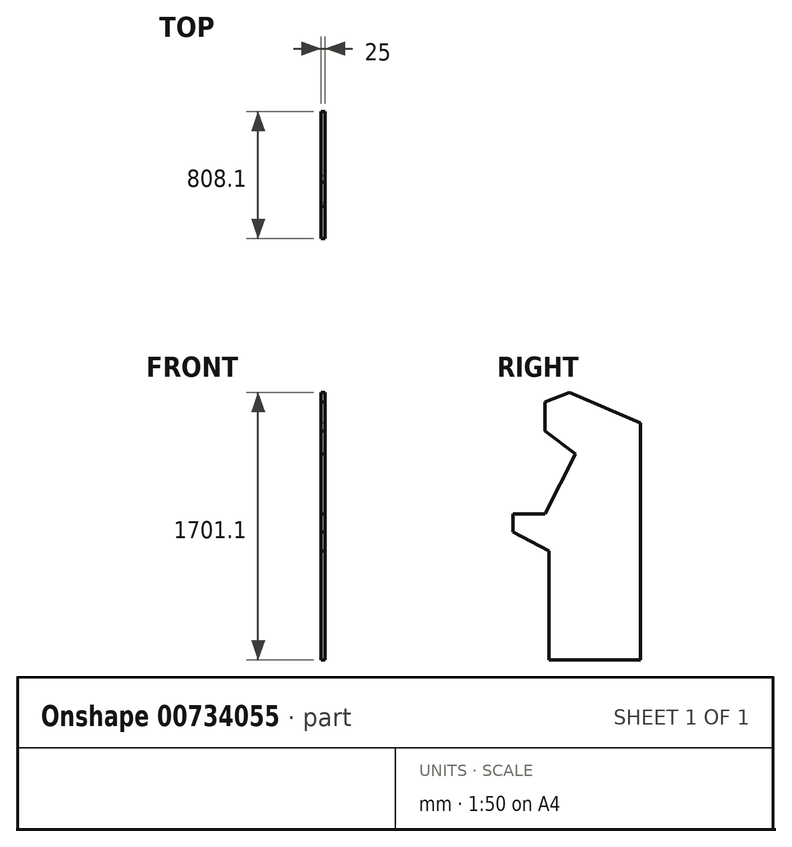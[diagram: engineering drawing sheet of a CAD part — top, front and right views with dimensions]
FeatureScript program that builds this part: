
annotation { "Feature Type Name" : "Feature", "Feature Type Description" : "" }
export const myFeature = defineFeature(function(context is Context, id is Id, definition is map)
    precondition{}
    {
        {
            var Q0;
            Q0=qCreatedBy(makeId("Right.planeOp"),FACE);
            var sketch = newSketch(context, id + "F0", { "sketchPlane" : qUnion([Q0])});
            skLineSegment(sketch, "E0.bottom", {"start": v(-132.1, -239.95) * mm, "end": v(447.9, -239.95) * mm});
            skLineSegment(sketch, "E0.left", {"start": v(-132.1, -239.95) * mm, "end": v(-132.1, 453.45) * mm});
            skLineSegment(sketch, "E1", {"start": v(-132.1, 453.45) * mm, "end": v(-360.2, 572.65) * mm});
            skLineSegment(sketch, "E2", {"start": v(-360.2, 572.65) * mm, "end": v(-360.2, 687.45) * mm});
            skLineSegment(sketch, "E3", {"start": v(-360.2, 687.45) * mm, "end": v(-156.4, 687.45) * mm});
            skLineSegment(sketch, "E4", {"start": v(-156.4, 687.45) * mm, "end": v(37.4, 1069.35) * mm});
            skLineSegment(sketch, "E5", {"start": v(37.4, 1069.35) * mm, "end": v(-156.4, 1215.75) * mm});
            skLineSegment(sketch, "E6", {"start": v(-156.4, 1215.75) * mm, "end": v(-156.4, 1399.45) * mm});
            skLineSegment(sketch, "E7", {"start": v(-156.4, 1399.45) * mm, "end": v(0, 1461.15) * mm});
            skLineSegment(sketch, "E8", {"start": v(0, 1461.15) * mm, "end": v(447.9, 1265.85) * mm});
            skLineSegment(sketch, "E9", {"start": v(447.9, 1265.85) * mm, "end": v(447.9, -239.95) * mm});
            skSolve(sketch);
        }
        {
            var Q0;
            Q0 = qSketchRegion(id + "F0", true);
            extrude(context, id + "F1", {"entities" : qUnion([Q0]), "depth" : 25 * mm, "offsetDistance" : 25 * mm});
        }
    });
